# Revit family: Bernhardt-Design_Occasional_Table_Albany
name_source: partatom
category: Furniture
units: mm (PartAtom-declared; Revit-internal decimal feet)

## family parameters
Always vertical = Yes
Cut with Voids When Loaded = No
OmniClass Number = 23.40.20.00
OmniClass Title = General Furniture and Specialties
Room Calculation Point = No
Shared = No
Work Plane-Based = No

## types (9) — shared parameters
Manufacturer = Bernhardt Design
Model = Albany
Tabletop Glass = Etched Grey Glass
URL = http://www.bernhardtdesign.com
zero-valued in all types: Default Elevation

## per-type parameters (varying)
| type | Base Finish | Base bottom radius | Base height | Base top radius | Catalog | Glass top | SKU | Table Glass | Table Mount radius | Table Wood | Table height | Tabletop bottom | Tabletop radius |
| Albany - ALS-A17 - 17" Glass - Graphite | Graphite - Brushed | 5.906 " | 16.929 " | 1.282 " | ALS-A17 | 17.521 " | ALS-A17 | Yes | 5.512 " | No | 18 " | 17.126 " | 8.5 " |
| Albany - ALS-A17 - 17" Wood - Graphite | Graphite - Brushed | 5.906 " | 16.929 " | 1.282 " | ALS-A17 | 17.521 " | ALS-A17 | No | 5.512 " | Yes | 18 " | 17.126 " | 8.5 " |
| Albany - ALS-A17 - 17" Wood - Brass | Brass - Brushed PVD | 5.906 " | 16.929 " | 1.282 " | ALS-A17 | 17.521 " | ALS-A17 | No | 5.512 " | Yes | 18 " | 17.126 " | 8.5 " |
| Albany - ALS-A21 - 21" Glass - Graphite | Graphite - Brushed | 7.48 " | 16.929 " | 2.184 " | ALS-A21 | 17.521 " | ALS-A21 | Yes | 6.693 " | No | 18 " | 17.126 " | 10.5 " |
| Albany - ALS-A21 - 21" Wood - Graphite | Graphite - Brushed | 7.48 " | 16.929 " | 2.184 " | ALS-A21 | 17.521 " | ALS-A21 | No | 6.693 " | Yes | 18 " | 17.126 " | 10.5 " |
| Albany - ALS-A21 - 21" Wood - Brass | Brass - Brushed PVD | 7.48 " | 16.929 " | 2.184 " | ALS-A21 | 17.521 " | ALS-A21 | No | 6.693 " | Yes | 18 " | 17.126 " | 10.5 " |
| Albany - ALS-A42 - 42" Glass - Graphite | Graphite - Brushed | 10.728 " | 13.976 " | 4.731 " | ALS-A42 | 14.568 " | ALS-A42 | Yes | 11.811 " | No | 15.047 " | 14.173 " | 21 " |
| Albany - ALS-A42 - 42" Wood - Graphite | Graphite - Brushed | 10.728 " | 13.976 " | 4.731 " | ALS-A42 | 14.568 " | ALS-A42 | No | 11.811 " | Yes | 15.047 " | 14.173 " | 21 " |
| Albany - ALS-A42 - 42" Wood - Brass | Brass - Brushed PVD | 10.728 " | 13.976 " | 4.731 " | ALS-A42 | 14.568 " | ALS-A42 | No | 11.811 " | Yes | 15.047 " | 14.173 " | 21 " |

## geometry (parser evidence)
native form markers: Sweep x5
no freeform markers — native parametric forms only
